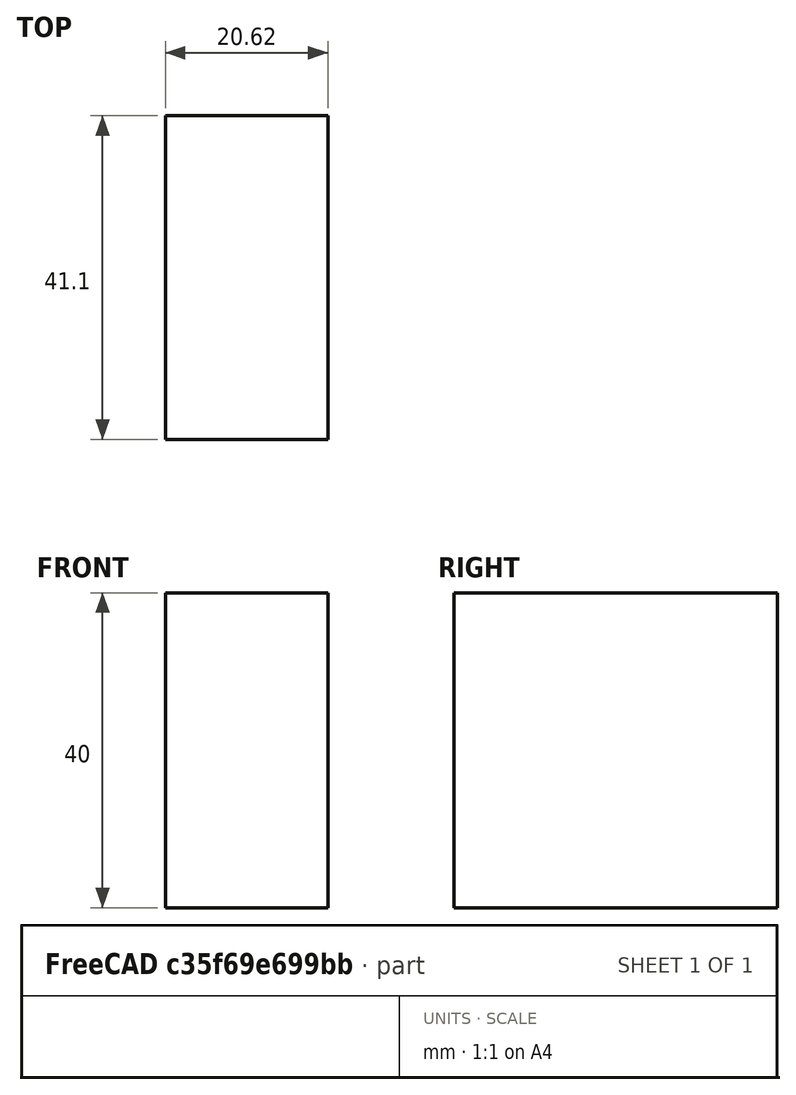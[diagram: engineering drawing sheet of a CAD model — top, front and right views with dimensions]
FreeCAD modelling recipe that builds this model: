
FCSTD DOCUMENT  (FreeCAD 1.1R20260325 (Git shallow))
Label: Tomada
License: All rights reserved
LicenseURL: https://en.wikipedia.org/wiki/All_rights_reserved
objects: App::Point×1, Sketcher::SketchObject×1, PartDesign::Pad×1, PartDesign::Body×1
note: 6 computed .brp shape members not serialized (recipe doc carries the construction recipe); baked Part::Feature solids carry a one-line shape summary decoded from their .brp

FEATURE [App::Point] Origin001
  Role = Origin
FEATURE [Sketcher::SketchObject] Sketch
  ArcFitTolerance = 1e-06
  AttachmentSupport = -> [Origin]
  ExternalTypes = [0]
  FullyConstrained = false
  MakeInternals = false
  MapMode = 5
  _ExternalGeoVersion = 1
  sketch-geometry (5):
    g0: LineSegment StartX=-10.3085 StartY=20.5467 StartZ=0 EndX=-10.3085 EndY=-20.5467 EndZ=0
    g1: LineSegment StartX=-10.3085 StartY=-20.5467 StartZ=0 EndX=10.3085 EndY=-20.5467 EndZ=0
    g2: LineSegment StartX=10.3085 StartY=-20.5467 StartZ=0 EndX=10.3085 EndY=20.5467 EndZ=0
    g3: LineSegment StartX=10.3085 StartY=20.5467 StartZ=0 EndX=-10.3085 EndY=20.5467 EndZ=0
    g4: GeomPoint [constr] X=0 Y=0 Z=0
  constraints (10):
    c: Coincident(g0,g1)
    c: Coincident(g1,g2)
    c: Coincident(g2,g3)
    c: Coincident(g3,g0)
    c: Vertical(g0)
    c: Vertical(g2)
    c: Horizontal(g1)
    c: Horizontal(g3)
    c: Symmetric(g2,g0,g4)
    c: Coincident(g4,g-1)
FEATURE [PartDesign::Pad] Pad
  Direction = (0,0,1)
  Length = 37
  Length2 = 10
  Profile = -> Sketch
  ReferenceAxis = -> Sketch [N_Axis]
  Refine = true
  SideType = 0
  Suppressed = false
  Type = 0
  Type2 = 0
FEATURE [PartDesign::Body] Body  label="Tomada"
  AllowCompound = false
  Group = -> [Sketch,Pad]
  Origin = -> Origin
  Tip = -> Pad
